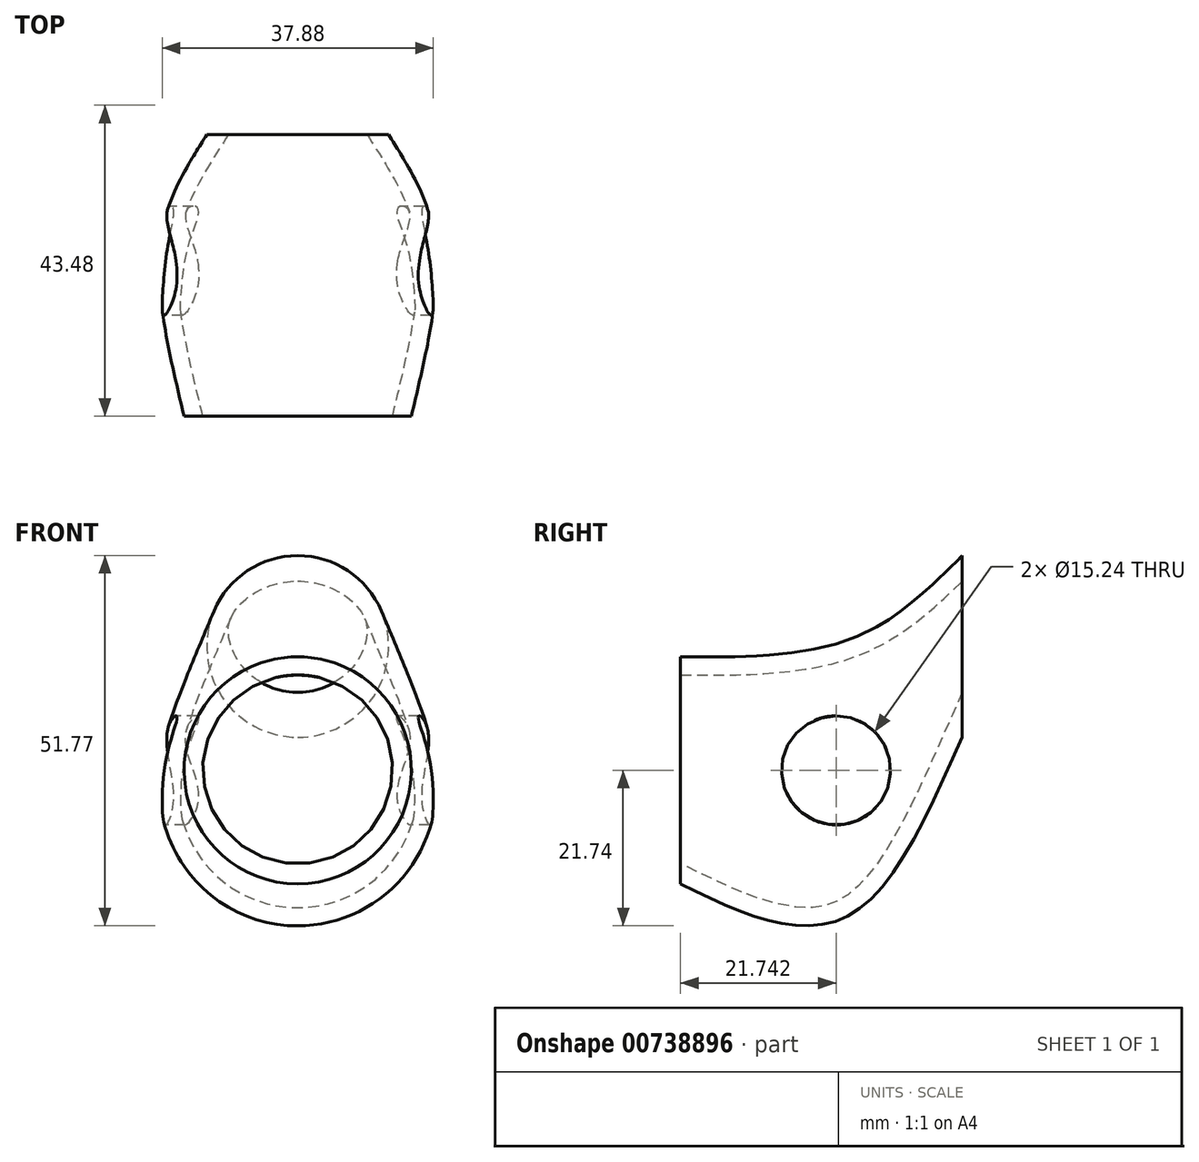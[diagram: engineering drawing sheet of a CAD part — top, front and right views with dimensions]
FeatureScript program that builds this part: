
annotation { "Feature Type Name" : "Feature", "Feature Type Description" : "" }
export const myFeature = defineFeature(function(context is Context, id is Id, definition is map)
    precondition{}
    {
        {
            var Q0;
            Q0=qCreatedBy(makeId("Front.planeOp"),FACE);
            cPlane(context, id + "F0", {"entities" : qUnion([Q0]), "cplaneType" : CPlaneType.OFFSET, "offset" : 25.4 * mm, "width" : 152.4 * mm, "height" : 152.4 * mm});
        }
        {
            var Q0;
            Q0=qCreatedBy(makeId("Front.planeOp"),FACE);
            var sketch = newSketch(context, id + "F1", { "sketchPlane" : qUnion([Q0])});
            skCircle(sketch, "E0", {"center": v(0, 0) * mm, "radius": 19.05 * mm});
            skSolve(sketch);
        }
        {
            var Q0;
            Q0=qCreatedBy(id+"F0.planeOp",FACE);
            var sketch = newSketch(context, id + "F2", { "sketchPlane" : qUnion([Q0])});
            skCircle(sketch, "E1", {"center": v(0, 0) * mm, "radius": 15.88 * mm});
            skSolve(sketch);
        }
        {
            var Q0;
            Q0=qCreatedBy(makeId("Right.planeOp"),FACE);
            cPlane(context, id + "F3", {"entities" : qUnion([Q0]), "cplaneType" : CPlaneType.OFFSET, "offset" : 25.4 * mm, "oppositeDirection" : true, "width" : 152.4 * mm, "height" : 152.4 * mm});
        }
        {
            var Q0;
            Q0=qCreatedBy(makeId("Front.planeOp"),FACE);
            cPlane(context, id + "F4", {"entities" : qUnion([Q0]), "cplaneType" : CPlaneType.OFFSET, "offset" : 13.97 * mm, "oppositeDirection" : true, "width" : 152.4 * mm, "height" : 152.4 * mm});
        }
        {
            var Q0;
            Q0=qCreatedBy(id+"F4.planeOp",FACE);
            var sketch = newSketch(context, id + "F5", { "sketchPlane" : qUnion([Q0])});
            skCircle(sketch, "E2", {"center": v(0, 17.33) * mm, "radius": 12.7 * mm});
            skSolve(sketch);
        }
        {
            var Q0;
            Q0=makeQuery(id+"F2.imprint","IMPRINT",FACE,{"disambiguationData":[TD([[makeQuery(id+"F2.imprint","IMPRINT",EDGE,{"derivedFrom":sQuery(id+"F2.wireOp",EDGE,"E1")}),1.0]])]});
            var Q1;
            Q1=makeQuery(id+"F1.imprint","IMPRINT",FACE,{"disambiguationData":[TD([[makeQuery(id+"F1.imprint","IMPRINT",EDGE,{"derivedFrom":sQuery(id+"F1.wireOp",EDGE,"E0")}),1.0]])]});
            var Q2;
            Q2=makeQuery(id+"F5.imprint","IMPRINT",FACE,{"disambiguationData":[TD([[makeQuery(id+"F5.imprint","IMPRINT",EDGE,{"derivedFrom":sQuery(id+"F5.wireOp",EDGE,"E2")}),1.0]])]});
            loft(context, id + "F6", {"sheetProfilesArray" : [{ "sheetProfileEntities" : qUnion([Q0]) }, { "sheetProfileEntities" : qUnion([Q1]) }, { "sheetProfileEntities" : qUnion([Q2]) }]});
        }
        {
            var Q0;
            Q0=makeQuery(id+"F6.opLoft","CAP_FACE",FACE,{"disambiguationData":[OSD([makeQuery(id+"F5.imprint","IMPRINT",FACE,{"disambiguationData":[TD([[makeQuery(id+"F5.imprint","IMPRINT",EDGE,{"derivedFrom":sQuery(id+"F5.wireOp",EDGE,"E2")}),1.0]])]})])],"isStart":true});
            var Q1;
            Q1=makeQuery(id+"F6.opLoft","CAP_FACE",FACE,{"disambiguationData":[OSD([makeQuery(id+"F2.imprint","IMPRINT",FACE,{"disambiguationData":[TD([[makeQuery(id+"F2.imprint","IMPRINT",EDGE,{"derivedFrom":sQuery(id+"F2.wireOp",EDGE,"E1")}),1.0]])]})])],"isStart":true});
            shell(context, id + "F7", {"entities" : qUnion([Q0, Q1]), "thickness" : 2.54 * mm});
        }
        {
            var Q0;
            Q0=qCreatedBy(id+"F3.planeOp",FACE);
            var sketch = newSketch(context, id + "F8", { "sketchPlane" : qUnion([Q0])});
            skCircle(sketch, "E3", {"center": v(-3.66, 0) * mm, "radius": 7.62 * mm});
            skSolve(sketch);
        }
        {
            var Q0;
            Q0 = qSketchRegion(id + "F8", true);
            extrude(context, id + "F9", {"entities" : qUnion([Q0]), "operationType" : NewBodyOperationType.REMOVE, "depth" : 50.8 * mm, "offsetDistance" : 25.4 * mm});
        }
    });
